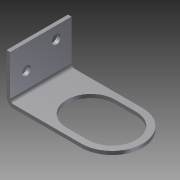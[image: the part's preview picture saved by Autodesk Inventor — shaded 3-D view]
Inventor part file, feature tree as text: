
AUTODESK INVENTOR PART (.ipt)
format: ipt  version: 2014 (Build 180170000, 170)  size: 122,368 bytes
history: native  units: mm (DEFAULTED — no unit token found)
features: sheet_metal_op x3, sketch x3, other x3, projected_geometry x1
ambient origin geometry x8: Origin, YZ Plane, XZ Plane, XY Plane, X Axis, Y Axis, Z Axis, Center Point
bodies: Solid1 (feature_tree)
feature tree (10):
  sheet_metal_op  "Face1"
  sheet_metal_op  "Flange1"
  sketch  "Sketch1"  dims[d0=38.0mm]
  other  "Plate1"
  sketch  "Sketch2"  dims[d1=63.0mm]
  other  "Plate2"
  sheet_metal_op  "Bend1"
  sketch  "Sketch3"  dims[d2=4.0mm d3=43.0mm d4=2.2mm d5=2.2mm d6=1.1mm d7=4.4mm d8=2.2mm d9=27.0mm d10=90.0deg d11=2.2mm d12=5.5mm d13=9.5mm d14=7.5mm d15=10.0mm d16=15.0mm d17=2.2mm d18=0.0mm]
  projected_geometry  "Projected Loop1"
  other  "Cut1"
